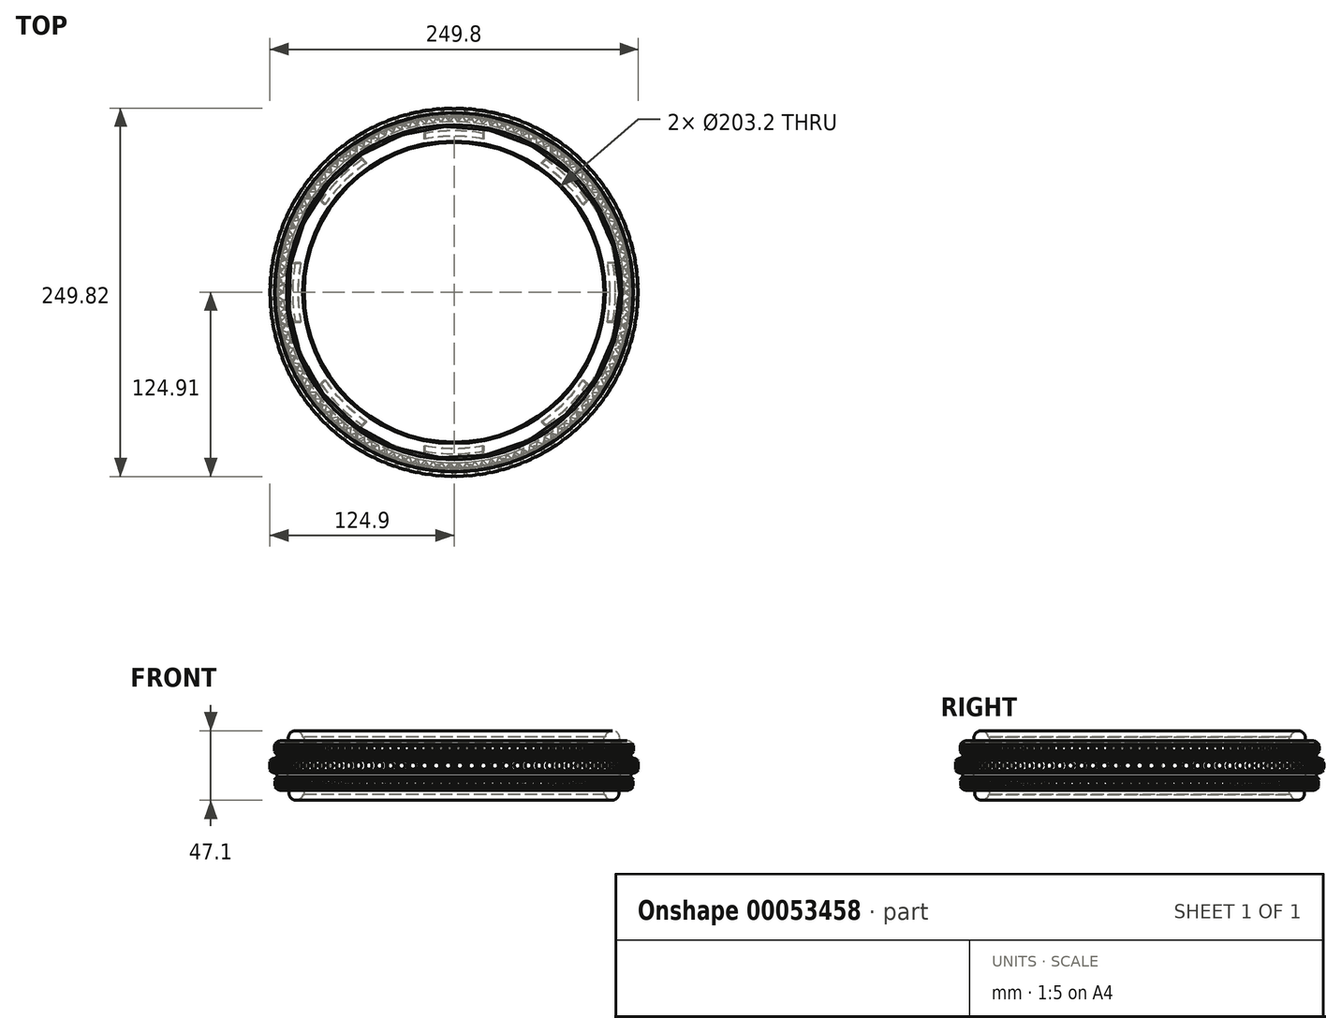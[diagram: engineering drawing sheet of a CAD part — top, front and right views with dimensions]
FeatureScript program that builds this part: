
annotation { "Feature Type Name" : "Feature", "Feature Type Description" : "" }
export const myFeature = defineFeature(function(context is Context, id is Id, definition is map)
    precondition{}
    {
        {
            var Q0;
            Q0=qCreatedBy(makeId("Front.planeOp"),FACE);
            var sketch = newSketch(context, id + "F0", { "sketchPlane" : qUnion([Q0])});
            skArc(sketch, "E0", {"start": v(101.6, -12.7) * mm, "mid": v(114.3, 0) * mm, "end": v(101.6, 12.7) * mm});
            skArc(sketch, "E1.0", {"start": v(101.6, -19.55) * mm, "mid": v(102.01, -19.54) * mm, "end": v(102.42, -19.53) * mm});
            skLineSegment(sketch, "E2", {"start": v(101.6, -19.55) * mm, "end": v(101.6, -12.7) * mm});
            skLineSegment(sketch, "E3", {"start": v(101.6, 12.7) * mm, "end": v(101.6, 19.55) * mm});
            skLineSegment(sketch, "E4", {"start": v(0, 32.33) * mm, "end": v(0, -30.54) * mm, "construction": true});
            skArc(sketch, "E5", {"start": v(120.5, -4.97) * mm, "mid": v(126.16, 0) * mm, "end": v(120.5, 4.97) * mm});
            skArc(sketch, "E6", {"start": v(119.7, 7.38) * mm, "mid": v(121.23, 14.8) * mm, "end": v(113.67, 15.37) * mm});
            skArc(sketch, "E7", {"start": v(113.71, -15.34) * mm, "mid": v(121.2, -14.78) * mm, "end": v(119.68, -7.43) * mm});
            skArc(sketch, "E8", {"start": v(102.42, -19.53) * mm, "mid": v(108.45, -23.32) * mm, "end": v(111.48, -16.87) * mm});
            skArc(sketch, "E9", {"start": v(111.96, 16.57) * mm, "mid": v(108.96, 23.36) * mm, "end": v(102.6, 19.52) * mm});
            skArc(sketch, "E10.trimOffspring", {"start": v(111.48, -16.87) * mm, "mid": v(112.62, -16.14) * mm, "end": v(113.71, -15.34) * mm});
            skArc(sketch, "E11.trimOffspring", {"start": v(119.68, -7.43) * mm, "mid": v(120.13, -6.21) * mm, "end": v(120.5, -4.97) * mm});
            skArc(sketch, "E12.trimOffspring", {"start": v(120.5, 4.97) * mm, "mid": v(120.14, 6.19) * mm, "end": v(119.7, 7.38) * mm});
            skArc(sketch, "E13.trimOffspring", {"start": v(113.67, 15.37) * mm, "mid": v(112.83, 16) * mm, "end": v(111.96, 16.57) * mm});
            skArc(sketch, "E14.trimOffspring", {"start": v(102.6, 19.52) * mm, "mid": v(102.1, 19.54) * mm, "end": v(101.6, 19.55) * mm});
            skSolve(sketch);
        }
        {
            var Q0;
            Q0 = qSketchRegion(id + "F0", true);
            var Q1;
            Q1=sQuery(id+"F0.wireOp",EDGE,"E4");
            revolve(context, id + "F1", {"entities" : qUnion([Q0]), "axis" : qUnion([Q1]), "revolveType" : RevolveType.FULL});
        }
        {
            var Q0;
            Q0=qCreatedBy(makeId("Front.planeOp"),FACE);
            var sketch = newSketch(context, id + "F2", { "sketchPlane" : qUnion([Q0])});
            skLineSegment(sketch, "E15.rect.bottom", {"start": v(126.4, 3.6) * mm, "end": v(115.64, 3.6) * mm});
            skLineSegment(sketch, "E15.rect.top", {"start": v(126.4, -3.6) * mm, "end": v(115.64, -3.6) * mm});
            skLineSegment(sketch, "E15.rect.left", {"start": v(126.4, 3.6) * mm, "end": v(126.4, -3.6) * mm});
            skLineSegment(sketch, "E15.rect.right", {"start": v(115.64, 3.6) * mm, "end": v(115.64, -3.6) * mm});
            skPoint(sketch, "E15.rect.middle", {"position": v(121.02, 0) * mm});
            skLineSegment(sketch, "E16", {"start": v(0, 23.36) * mm, "end": v(0, -22.16) * mm, "construction": true});
            skSolve(sketch);
        }
        {
            var Q0;
            Q0 = qSketchRegion(id + "F2", true);
            var Q1;
            Q1=sQuery(id+"F2.wireOp",EDGE,"E16");
            revolve(context, id + "F3", {"operationType" : NewBodyOperationType.REMOVE, "entities" : qUnion([Q0]), "axis" : qUnion([Q1]), "revolveType" : RevolveType.FULL, "oppositeDirection" : true});
        }
        {
            var Q0;
            Q0=qCreatedBy(makeId("Front.planeOp"),FACE);
            var sketch = newSketch(context, id + "F4", { "sketchPlane" : qUnion([Q0])});
            skLineSegment(sketch, "E17.rect.bottom", {"start": v(44.45, 3.05) * mm, "end": v(-44.45, 3.05) * mm});
            skLineSegment(sketch, "E17.rect.top", {"start": v(44.45, -3.05) * mm, "end": v(-44.45, -3.05) * mm});
            skLineSegment(sketch, "E17.rect.left", {"start": v(44.45, 3.05) * mm, "end": v(44.45, -3.05) * mm});
            skLineSegment(sketch, "E17.rect.right", {"start": v(-44.45, 3.05) * mm, "end": v(-44.45, -3.05) * mm});
            skPoint(sketch, "E17.rect.middle", {"position": v(0, 0) * mm});
            skSolve(sketch);
        }
        {
            var Q0;
            Q0 = qSketchRegion(id + "F4", true);
            extrude(context, id + "F5", {"entities" : qUnion([Q0]), "operationType" : NewBodyOperationType.REMOVE, "endBound" : BoundingType.THROUGH_ALL, "depth" : 25.4 * mm});
        }
        {
            var Q0;
            Q0=makeQuery(id+"F5.boolean.opBoolean","COPY",FACE,{"derivedFrom":makeQuery(id+"F5.opExtrude","SWEPT_FACE",FACE,{"disambiguationData":[OSD([sQuery(id+"F4.wireOp",EDGE,"E17.rect.bottom")])]})});
            var Q1;
            Q1=makeQuery(id+"F5.boolean.opBoolean","COPY",FACE,{"derivedFrom":makeQuery(id+"F5.opExtrude","SWEPT_FACE",FACE,{"disambiguationData":[OSD([sQuery(id+"F4.wireOp",EDGE,"E17.rect.top")])]})});
            var Q2;
            Q2=makeQuery(id+"F5.boolean.opBoolean","COPY",FACE,{"derivedFrom":makeQuery(id+"F5.opExtrude","SWEPT_FACE",FACE,{"disambiguationData":[OSD([sQuery(id+"F4.wireOp",EDGE,"E17.rect.right")])]})});
            var Q3;
            Q3=makeQuery(id+"F5.boolean.opBoolean","COPY",FACE,{"derivedFrom":makeQuery(id+"F5.opExtrude","SWEPT_FACE",FACE,{"disambiguationData":[OSD([sQuery(id+"F4.wireOp",EDGE,"E17.rect.left")])]})});
            var Q4;
            Q4=sQuery(id+"F2.wireOp",EDGE,"E16");
            circularPattern(context, id + "F6", {"operationType" : NewBodyOperationType.ADD, "faces" : qUnion([Q0, Q1, Q2, Q3]), "axis" : qUnion([Q4]), "angle" : 360 * degree, "instanceCount" : 6, "equalSpace" : true, "patternType" : PatternType.FACE});
        }
        {
            var Q0;
            Q0=qCreatedBy(makeId("Front.planeOp"),FACE);
            var sketch = newSketch(context, id + "F7", { "sketchPlane" : qUnion([Q0])});
            skLineSegment(sketch, "E18", {"start": v(109.28, 0) * mm, "end": v(124.9, 0) * mm});
            skLineSegment(sketch, "E19", {"start": v(124.9, 0) * mm, "end": v(124.9, 2.47) * mm});
            skLineSegment(sketch, "E20", {"start": v(124.9, 2.47) * mm, "end": v(121.57, 3.76) * mm});
            skLineSegment(sketch, "E21", {"start": v(121.57, 3.76) * mm, "end": v(117.09, 0) * mm});
            skLineSegment(sketch, "E22", {"start": v(117.09, 0) * mm, "end": v(132.71, 0) * mm, "construction": true});
            skPoint(sketch, "E22.endSnap0", {"position": v(117.09, 0) * mm});
            skSolve(sketch);
        }
        {
            var Q0;
            Q0 = qSketchRegion(id + "F7", true);
            var Q1;
            Q1=sQuery(id+"F7.wireOp",EDGE,"E22");
            revolve(context, id + "F8", {"entities" : qUnion([Q0]), "axis" : qUnion([Q1]), "revolveType" : RevolveType.FULL});
        }
        {
            var Q0;
            Q0=makeQuery(id+"F8.opRevolve","SWEPT_BODY",BODY,{"disambiguationData":[OSD([sQuery(id+"F7.wireOp",EDGE,"E18"),sQuery(id+"F7.wireOp",EDGE,"E19"),sQuery(id+"F7.wireOp",EDGE,"E20"),sQuery(id+"F7.wireOp",EDGE,"E21")])]});
            var Q1;
            Q1=sQuery(id+"F2.wireOp",EDGE,"E16");
            circularPattern(context, id + "F9", {"entities" : qUnion([Q0]), "axis" : qUnion([Q1]), "angle" : 360 * degree, "instanceCount" : 98, "equalSpace" : true});
        }
        {
            var Q0;
            Q0=qCreatedBy(makeId("Front.planeOp"),FACE);
            var sketch = newSketch(context, id + "F10", { "sketchPlane" : qUnion([Q0])});
            skLineSegment(sketch, "E23.rect.bottom", {"start": v(123.35, 14.38) * mm, "end": v(112.65, 14.38) * mm});
            skLineSegment(sketch, "E23.rect.top", {"start": v(123.35, 9.3) * mm, "end": v(112.65, 9.3) * mm});
            skLineSegment(sketch, "E23.rect.left", {"start": v(123.35, 14.38) * mm, "end": v(123.35, 9.3) * mm});
            skLineSegment(sketch, "E23.rect.right", {"start": v(112.65, 14.38) * mm, "end": v(112.65, 9.3) * mm});
            skPoint(sketch, "E23.rect.middle", {"position": v(118, 11.84) * mm});
            skLineSegment(sketch, "E24.rect.bottom", {"start": v(122.88, -14.58) * mm, "end": v(113.12, -14.58) * mm});
            skLineSegment(sketch, "E24.rect.top", {"start": v(122.88, -9.5) * mm, "end": v(113.12, -9.5) * mm});
            skLineSegment(sketch, "E24.rect.left", {"start": v(122.88, -14.58) * mm, "end": v(122.88, -9.5) * mm});
            skLineSegment(sketch, "E24.rect.right", {"start": v(113.12, -14.58) * mm, "end": v(113.12, -9.5) * mm});
            skPoint(sketch, "E24.rect.middle", {"position": v(118, -12.04) * mm});
            skLineSegment(sketch, "E25", {"start": v(118, 20.33) * mm, "end": v(118, -19.78) * mm, "construction": true});
            skSolve(sketch);
        }
        {
            var Q0;
            Q0=qCreatedBy(makeId("Front.planeOp"),FACE);
            var sketch = newSketch(context, id + "F11", { "sketchPlane" : qUnion([Q0])});
            skLineSegment(sketch, "E26", {"start": v(0, 42.8) * mm, "end": v(0, -35.28) * mm, "construction": true});
            skSolve(sketch);
        }
        {
            var Q0;
            Q0 = qSketchRegion(id + "F10", true);
            var Q1;
            Q1=sQuery(id+"F11.wireOp",EDGE,"E26");
            revolve(context, id + "F12", {"operationType" : NewBodyOperationType.REMOVE, "entities" : qUnion([Q0]), "axis" : qUnion([Q1]), "revolveType" : RevolveType.FULL, "oppositeDirection" : true});
        }
        {
            var Q0;
            Q0=qCreatedBy(makeId("Front.planeOp"),FACE);
            var sketch = newSketch(context, id + "F13", { "sketchPlane" : qUnion([Q0])});
            skLineSegment(sketch, "E27.rect.bottom", {"start": v(20.14, 11.94) * mm, "end": v(-20.14, 11.94) * mm});
            skLineSegment(sketch, "E27.rect.top", {"start": v(20.14, 9.9) * mm, "end": v(-20.14, 9.9) * mm});
            skLineSegment(sketch, "E27.rect.left", {"start": v(20.14, 11.94) * mm, "end": v(20.14, 9.9) * mm});
            skLineSegment(sketch, "E27.rect.right", {"start": v(-20.14, 11.94) * mm, "end": v(-20.14, 9.9) * mm});
            skPoint(sketch, "E27.rect.middle", {"position": v(0, 10.92) * mm});
            skLineSegment(sketch, "E28.rect.bottom", {"start": v(19.56, -9.96) * mm, "end": v(-19.56, -9.96) * mm});
            skLineSegment(sketch, "E28.rect.top", {"start": v(19.56, -12) * mm, "end": v(-19.56, -12) * mm});
            skLineSegment(sketch, "E28.rect.left", {"start": v(19.56, -9.96) * mm, "end": v(19.56, -12) * mm});
            skLineSegment(sketch, "E28.rect.right", {"start": v(-19.56, -9.96) * mm, "end": v(-19.56, -12) * mm});
            skPoint(sketch, "E28.rect.middle", {"position": v(0, -10.98) * mm});
            skSolve(sketch);
        }
        {
            var Q0;
            Q0 = qSketchRegion(id + "F13", true);
            extrude(context, id + "F14", {"entities" : qUnion([Q0]), "operationType" : NewBodyOperationType.REMOVE, "depth" : 127 * mm});
        }
        {
            var Q0;
            Q0=makeQuery(id+"F14.boolean.opBoolean","COPY",FACE,{"derivedFrom":makeQuery(id+"F14.opExtrude","SWEPT_FACE",FACE,{"disambiguationData":[OSD([sQuery(id+"F13.wireOp",EDGE,"E28.rect.bottom")])]})});
            var Q1;
            Q1=makeQuery(id+"F14.boolean.opBoolean","COPY",FACE,{"derivedFrom":makeQuery(id+"F14.opExtrude","SWEPT_FACE",FACE,{"disambiguationData":[OSD([sQuery(id+"F13.wireOp",EDGE,"E27.rect.bottom")])]})});
            var Q2;
            Q2=makeQuery(id+"F14.boolean.opBoolean","COPY",FACE,{"derivedFrom":makeQuery(id+"F14.opExtrude","SWEPT_FACE",FACE,{"disambiguationData":[OSD([sQuery(id+"F13.wireOp",EDGE,"E28.rect.top")])]})});
            var Q3;
            Q3=makeQuery(id+"F14.boolean.opBoolean","COPY",FACE,{"derivedFrom":makeQuery(id+"F14.opExtrude","SWEPT_FACE",FACE,{"disambiguationData":[OSD([sQuery(id+"F13.wireOp",EDGE,"E28.rect.right")])]})});
            var Q4;
            Q4=makeQuery(id+"F14.boolean.opBoolean","COPY",FACE,{"derivedFrom":makeQuery(id+"F14.opExtrude","SWEPT_FACE",FACE,{"disambiguationData":[OSD([sQuery(id+"F13.wireOp",EDGE,"E27.rect.right")])]})});
            var Q5;
            Q5=makeQuery(id+"F14.boolean.opBoolean","COPY",FACE,{"derivedFrom":makeQuery(id+"F14.opExtrude","SWEPT_FACE",FACE,{"disambiguationData":[OSD([sQuery(id+"F13.wireOp",EDGE,"E27.rect.top")])]})});
            var Q6;
            Q6=makeQuery(id+"F14.boolean.opBoolean","COPY",FACE,{"derivedFrom":makeQuery(id+"F14.opExtrude","SWEPT_FACE",FACE,{"disambiguationData":[OSD([sQuery(id+"F13.wireOp",EDGE,"E28.rect.left")])]})});
            var Q7;
            Q7=makeQuery(id+"F14.boolean.opBoolean","COPY",FACE,{"derivedFrom":makeQuery(id+"F14.opExtrude","SWEPT_FACE",FACE,{"disambiguationData":[OSD([sQuery(id+"F13.wireOp",EDGE,"E27.rect.left")])]})});
            var Q8;
            Q8=sQuery(id+"F11.wireOp",EDGE,"E26");
            circularPattern(context, id + "F15", {"faces" : qUnion([Q0, Q1, Q2, Q3, Q4, Q5, Q6, Q7]), "axis" : qUnion([Q8]), "angle" : 360 * degree, "instanceCount" : 8, "equalSpace" : true, "patternType" : PatternType.FACE});
        }
        {
            var Q0;
            Q0=qCreatedBy(makeId("Front.planeOp"),FACE);
            var sketch = newSketch(context, id + "F16", { "sketchPlane" : qUnion([Q0])});
            skLineSegment(sketch, "E29", {"start": v(109.2, 11.81) * mm, "end": v(123.43, 11.81) * mm, "construction": true});
            skLineSegment(sketch, "E30", {"start": v(121.74, 11.81) * mm, "end": v(121.74, 13.7) * mm});
            skLineSegment(sketch, "E31", {"start": v(121.74, 13.7) * mm, "end": v(119.42, 14.42) * mm});
            skLineSegment(sketch, "E32", {"start": v(119.42, 14.42) * mm, "end": v(115.75, 11.81) * mm});
            skLineSegment(sketch, "E33", {"start": v(115.75, 11.81) * mm, "end": v(121.74, 11.81) * mm});
            skSolve(sketch);
        }
        {
            var Q0;
            Q0 = qSketchRegion(id + "F16", true);
            var Q1;
            Q1=sQuery(id+"F16.wireOp",EDGE,"E29");
            revolve(context, id + "F17", {"entities" : qUnion([Q0]), "axis" : qUnion([Q1]), "revolveType" : RevolveType.FULL});
        }
        {
            var Q0;
            Q0=makeQuery(id+"F17.opRevolve","SWEPT_BODY",BODY,{"disambiguationData":[OSD([sQuery(id+"F16.wireOp",EDGE,"E30"),sQuery(id+"F16.wireOp",EDGE,"E31"),sQuery(id+"F16.wireOp",EDGE,"E32"),sQuery(id+"F16.wireOp",EDGE,"E33")])]});
            var Q1;
            Q1=sQuery(id+"F11.wireOp",EDGE,"E26");
            circularPattern(context, id + "F18", {"entities" : qUnion([Q0]), "axis" : qUnion([Q1]), "angle" : 360 * degree, "instanceCount" : 130, "equalSpace" : true});
        }
        {
            var Q0;
            Q0=qCreatedBy(makeId("Front.planeOp"),FACE);
            var sketch = newSketch(context, id + "F19", { "sketchPlane" : qUnion([Q0])});
            skLineSegment(sketch, "E34", {"start": v(115.55, -12.1) * mm, "end": v(121.35, -12.1) * mm});
            skLineSegment(sketch, "E35", {"start": v(121.35, -12.1) * mm, "end": v(121.35, -10.47) * mm});
            skLineSegment(sketch, "E36", {"start": v(121.35, -10.47) * mm, "end": v(119.15, -9.54) * mm});
            skLineSegment(sketch, "E37", {"start": v(119.15, -9.54) * mm, "end": v(115.55, -12.1) * mm});
            skLineSegment(sketch, "E38", {"start": v(112.19, -12.1) * mm, "end": v(123.2, -12.1) * mm, "construction": true});
            skSolve(sketch);
        }
        {
            var Q0;
            Q0 = qSketchRegion(id + "F19", true);
            var Q1;
            Q1=sQuery(id+"F19.wireOp",EDGE,"E38");
            revolve(context, id + "F20", {"entities" : qUnion([Q0]), "axis" : qUnion([Q1]), "revolveType" : RevolveType.FULL});
        }
        {
            var Q0;
            Q0=makeQuery(id+"F20.opRevolve","SWEPT_BODY",BODY,{"disambiguationData":[OSD([sQuery(id+"F19.wireOp",EDGE,"E34"),sQuery(id+"F19.wireOp",EDGE,"E35"),sQuery(id+"F19.wireOp",EDGE,"E36"),sQuery(id+"F19.wireOp",EDGE,"E37")])]});
            var Q1;
            Q1=sQuery(id+"F11.wireOp",EDGE,"E26");
            circularPattern(context, id + "F21", {"entities" : qUnion([Q0]), "axis" : qUnion([Q1]), "angle" : 360 * degree, "instanceCount" : 130, "equalSpace" : true});
        }
    });
